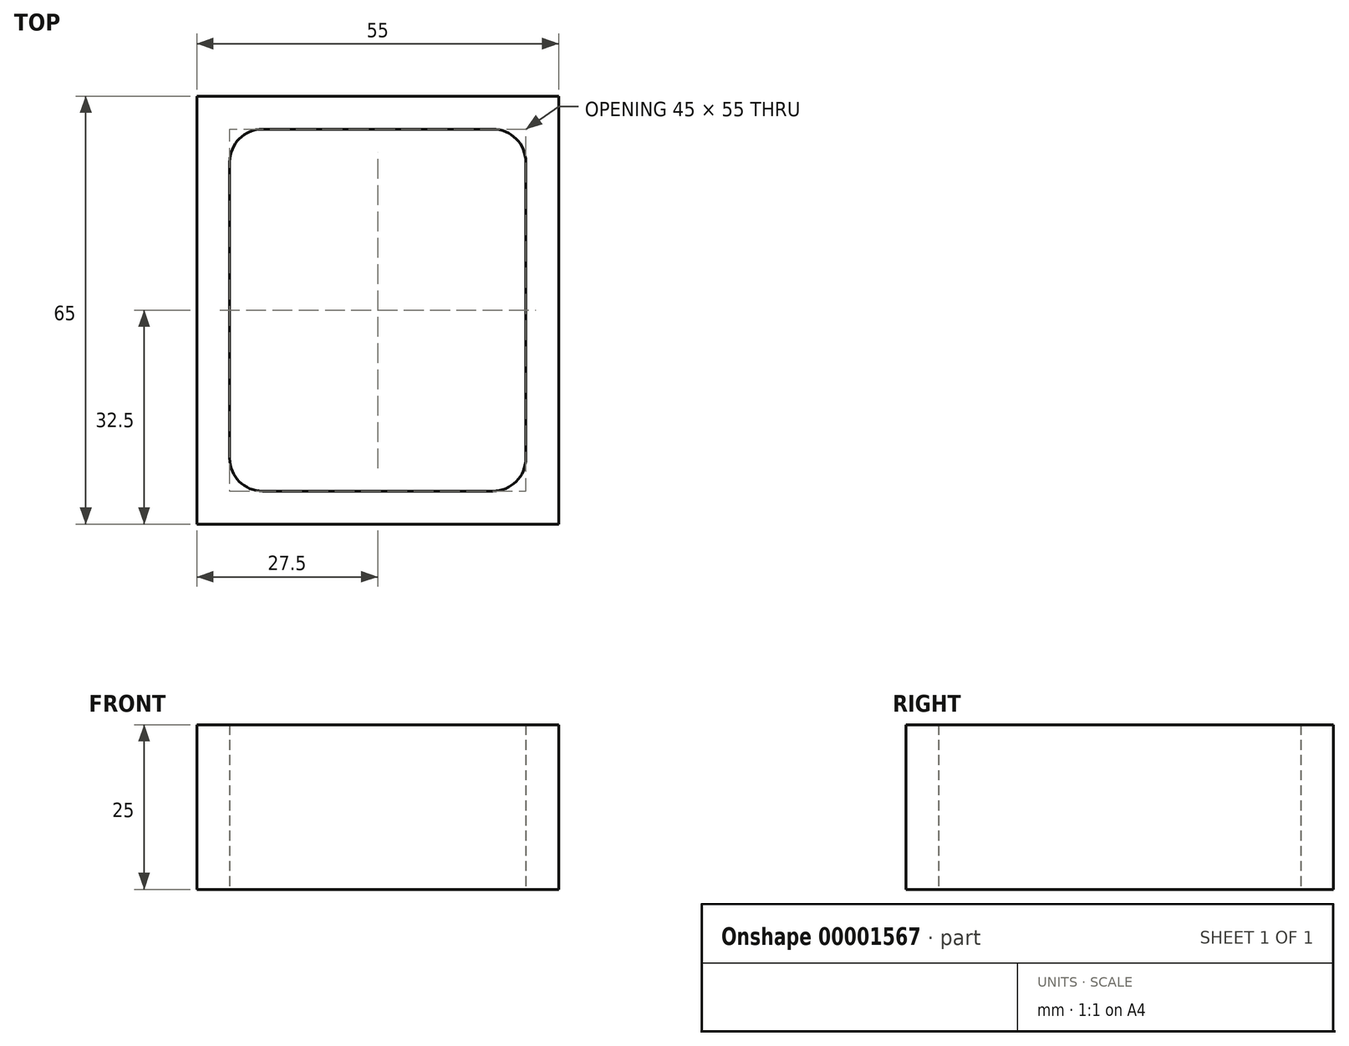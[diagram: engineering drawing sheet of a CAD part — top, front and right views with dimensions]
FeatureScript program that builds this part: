
annotation { "Feature Type Name" : "Feature", "Feature Type Description" : "" }
export const myFeature = defineFeature(function(context is Context, id is Id, definition is map)
    precondition{}
    {
        {
            var Q0;
            Q0=qCreatedBy(makeId("Top.planeOp"),FACE);
            var sketch = newSketch(context, id + "F0", { "sketchPlane" : qUnion([Q0])});
            skLineSegment(sketch, "E0.bottom", {"start": v(0, 0) * mm, "end": v(55, 0) * mm});
            skLineSegment(sketch, "E0.top", {"start": v(0, 65) * mm, "end": v(55, 65) * mm});
            skLineSegment(sketch, "E0.left", {"start": v(0, 0) * mm, "end": v(0, 65) * mm});
            skLineSegment(sketch, "E0.right", {"start": v(55, 0) * mm, "end": v(55, 65) * mm});
            skLineSegment(sketch, "E1.bottom", {"start": v(5, 60) * mm, "end": v(50, 60) * mm});
            skLineSegment(sketch, "E1.top", {"start": v(5, 5) * mm, "end": v(50, 5) * mm});
            skLineSegment(sketch, "E1.left", {"start": v(5, 60) * mm, "end": v(5, 5) * mm});
            skLineSegment(sketch, "E1.right", {"start": v(50, 60) * mm, "end": v(50, 5) * mm});
            skSolve(sketch);
        }
        {
            var Q0;
            Q0=makeQuery(id+"F0.imprint","IMPRINT",FACE,{"disambiguationData":[TD([[makeQuery(id+"F0.imprint","IMPRINT",EDGE,{"derivedFrom":sQuery(id+"F0.wireOp",EDGE,"E0.bottom")}),1.0]])]});
            extrude(context, id + "F1", {"entities" : qUnion([Q0]), "depth" : 25 * mm});
        }
        {
            var Q0;
            Q0=makeQuery(id+"F1.opExtrude","SWEPT_EDGE",EDGE,{"disambiguationData":[OSD([sQuery(id+"F0.wireOp",EDGE,"E1.bottom"),sQuery(id+"F0.wireOp",EDGE,"E1.right")])]});
            var Q1;
            Q1=makeQuery(id+"F1.opExtrude","SWEPT_EDGE",EDGE,{"disambiguationData":[OSD([sQuery(id+"F0.wireOp",EDGE,"E1.top"),sQuery(id+"F0.wireOp",EDGE,"E1.left")])]});
            var Q2;
            Q2=makeQuery(id+"F1.opExtrude","SWEPT_EDGE",EDGE,{"disambiguationData":[OSD([sQuery(id+"F0.wireOp",EDGE,"E1.top"),sQuery(id+"F0.wireOp",EDGE,"E1.right")])]});
            var Q3;
            Q3=makeQuery(id+"F1.opExtrude","SWEPT_EDGE",EDGE,{"disambiguationData":[OSD([sQuery(id+"F0.wireOp",EDGE,"E1.bottom"),sQuery(id+"F0.wireOp",EDGE,"E1.left")])]});
            fillet(context, id + "F2", {"entities" : qUnion([Q0, Q1, Q2, Q3]), "radius" : 5 * mm, "tangentPropagation" : true, "allowEdgeOverflow" : false});
        }
    });
